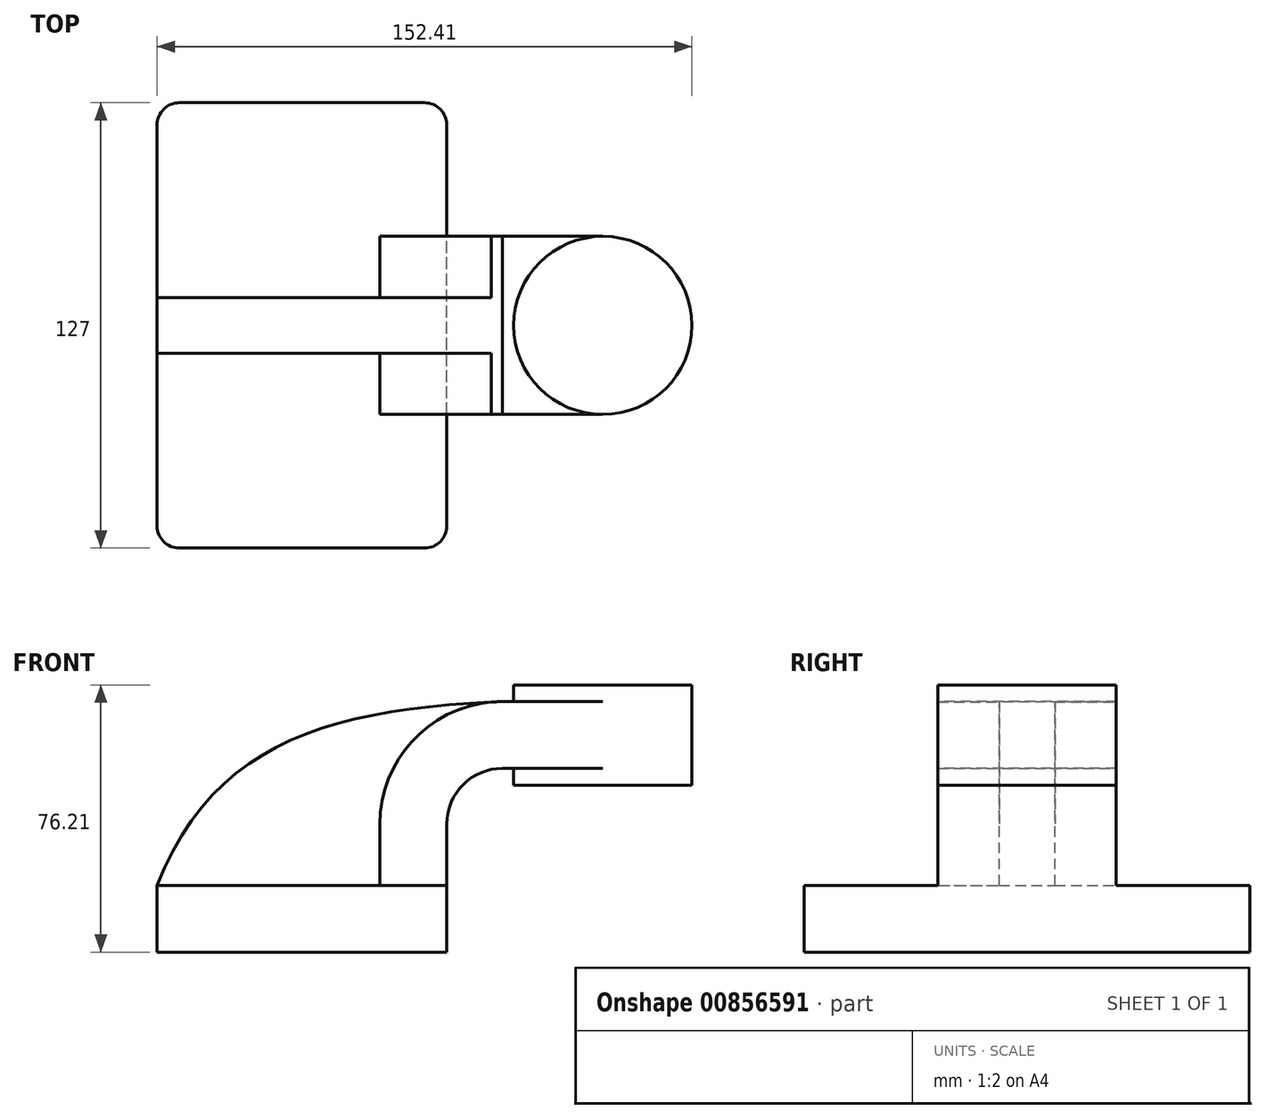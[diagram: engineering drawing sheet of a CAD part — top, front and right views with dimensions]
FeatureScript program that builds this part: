
annotation { "Feature Type Name" : "Feature", "Feature Type Description" : "" }
export const myFeature = defineFeature(function(context is Context, id is Id, definition is map)
    precondition{}
    {
        {
            var Q0;
            Q0=qCreatedBy(makeId("Front.planeOp"),FACE);
            var sketch = newSketch(context, id + "F0", { "sketchPlane" : qUnion([Q0])});
            skLineSegment(sketch, "E0.bottom", {"start": v(-41.28, 9.52) * mm, "end": v(41.27, 9.53) * mm});
            skLineSegment(sketch, "E0.top", {"start": v(-41.28, -9.53) * mm, "end": v(41.28, -9.53) * mm});
            skLineSegment(sketch, "E0.left", {"start": v(-41.28, 9.52) * mm, "end": v(-41.28, -9.53) * mm});
            skLineSegment(sketch, "E0.right", {"start": v(41.27, 9.53) * mm, "end": v(41.28, -9.52) * mm});
            skPoint(sketch, "E0.middle", {"position": v(0, 0) * mm});
            skLineSegment(sketch, "E1.bottom", {"start": v(111.12, 38.1) * mm, "end": v(60.32, 38.1) * mm});
            skLineSegment(sketch, "E1.top", {"start": v(111.12, 66.68) * mm, "end": v(60.32, 66.68) * mm});
            skLineSegment(sketch, "E1.left", {"start": v(111.12, 38.1) * mm, "end": v(111.12, 66.68) * mm});
            skLineSegment(sketch, "E1.right", {"start": v(60.32, 38.1) * mm, "end": v(60.32, 66.68) * mm});
            skPoint(sketch, "E1.middle", {"position": v(85.72, 52.39) * mm});
            skLineSegment(sketch, "E2", {"start": v(41.27, 9.53) * mm, "end": v(41.27, 27) * mm});
            skArc(sketch, "E3", {"start": v(41.27, 27) * mm, "mid": v(45.92, 38.23) * mm, "end": v(57.15, 42.88) * mm});
            skLineSegment(sketch, "E4", {"start": v(57.15, 42.88) * mm, "end": v(85.72, 42.88) * mm});
            skLineSegment(sketch, "E5.0", {"start": v(57.15, 61.93) * mm, "end": v(85.72, 61.93) * mm});
            skArc(sketch, "E5.1", {"start": v(22.22, 27) * mm, "mid": v(32.45, 51.7) * mm, "end": v(57.15, 61.93) * mm});
            skLineSegment(sketch, "E5.2", {"start": v(22.22, 9.53) * mm, "end": v(22.22, 27) * mm});
            skFitSpline(sketch, "E6", {"points": [v(-41.28, 9.52) * mm, v(57.15, 61.93) * mm], "startDerivative": vector(49, 123.52) * mm, "endDerivative": vector(146.93, 6.18) * mm});
            skLineSegment(sketch, "E7", {"start": v(85.72, 66.68) * mm, "end": v(85.72, 38.1) * mm});
            skSolve(sketch);
        }
        {
            var Q0;
            Q0=makeQuery(id+"F0.imprint","IMPRINT",FACE,{"disambiguationData":[TD([[makeQuery(id+"F0.imprint","IMPRINT",EDGE,{"derivedFrom":sQuery(id+"F0.wireOp",EDGE,"E0.top")}),1.0]])]});
            extrude(context, id + "F1", {"entities" : qUnion([Q0]), "endBound" : BoundingType.SYMMETRIC, "depth" : 127 * mm, "offsetDistance" : 25.4 * mm});
        }
        {
            var Q0;
            {var subQ1=sQuery(id+"F0.wireOp",EDGE,"E2");Q0=makeQuery(id+"F0.imprint","IMPRINT",FACE,{"disambiguationData":[TD([[makeQuery(id+"F0.imprint","IMPRINT",EDGE,{"derivedFrom":subQ1}),1.0]])]});}
            var Q1;
            {var subQ0=sQuery(id+"F0.wireOp",EDGE,"E4");var subQ1=sQuery(id+"F0.wireOp",EDGE,"E1.right");var subQ2=makeQuery(id+"F0.imprint","INTERSECT",VERTEX,{"derivedFrom":[subQ1,subQ0]});Q1=makeQuery(id+"F0.imprint","IMPRINT",FACE,{"disambiguationData":[TD([[makeQuery(id+"F0.imprint","IMPRINT",EDGE,{"disambiguationData":[TD([[subQ2,-1.0]])],"derivedFrom":subQ1}),-1.0]])]});}
            extrude(context, id + "F2", {"entities" : qUnion([Q0, Q1]), "operationType" : NewBodyOperationType.ADD, "endBound" : BoundingType.SYMMETRIC, "depth" : 50.8 * mm, "offsetDistance" : 25.4 * mm});
        }
        {
            var Q0;
            {var subQ3=sQuery(id+"F0.wireOp",EDGE,"E5.2");Q0=makeQuery(id+"F0.imprint","IMPRINT",FACE,{"disambiguationData":[TD([[makeQuery(id+"F0.imprint","IMPRINT",EDGE,{"derivedFrom":subQ3}),1.0]])]});}
            extrude(context, id + "F3", {"entities" : qUnion([Q0]), "operationType" : NewBodyOperationType.ADD, "endBound" : BoundingType.SYMMETRIC, "depth" : 15.88 * mm, "offsetDistance" : 25.4 * mm});
        }
        {
            var Q0;
            {var subQ4=sQuery(id+"F0.wireOp",EDGE,"E1.left");Q0=makeQuery(id+"F0.imprint","IMPRINT",FACE,{"disambiguationData":[TD([[makeQuery(id+"F0.imprint","IMPRINT",EDGE,{"derivedFrom":subQ4}),1.0]])]});}
            var Q1;
            Q1=sQuery(id+"F0.wireOp",EDGE,"E7");
            revolve(context, id + "F4", {"operationType" : NewBodyOperationType.ADD, "surfaceOperationType" : NewSurfaceOperationType.NEW, "entities" : qUnion([Q0]), "axis" : qUnion([Q1]), "revolveType" : RevolveType.FULL});
        }
        {
            var Q0;
            Q0=makeQuery(id+"F1.opExtrude","CAP_EDGE",EDGE,{"disambiguationData":[OSD([sQuery(id+"F0.wireOp",EDGE,"E0.left")])],"isStart":true});
            var Q1;
            Q1=makeQuery(id+"F1.opExtrude","CAP_EDGE",EDGE,{"disambiguationData":[OSD([sQuery(id+"F0.wireOp",EDGE,"E0.right")])],"isStart":true});
            var Q2;
            Q2=makeQuery(id+"F1.opExtrude","CAP_EDGE",EDGE,{"disambiguationData":[OSD([sQuery(id+"F0.wireOp",EDGE,"E0.left")])],"isStart":false});
            var Q3;
            Q3=makeQuery(id+"F1.opExtrude","CAP_EDGE",EDGE,{"disambiguationData":[OSD([sQuery(id+"F0.wireOp",EDGE,"E0.right")])],"isStart":false});
            fillet(context, id + "F5", {"entities" : qUnion([Q0, Q1, Q2, Q3]), "radius" : 6.35 * mm, "tangentPropagation" : true, "allowEdgeOverflow" : false});
        }
    });
